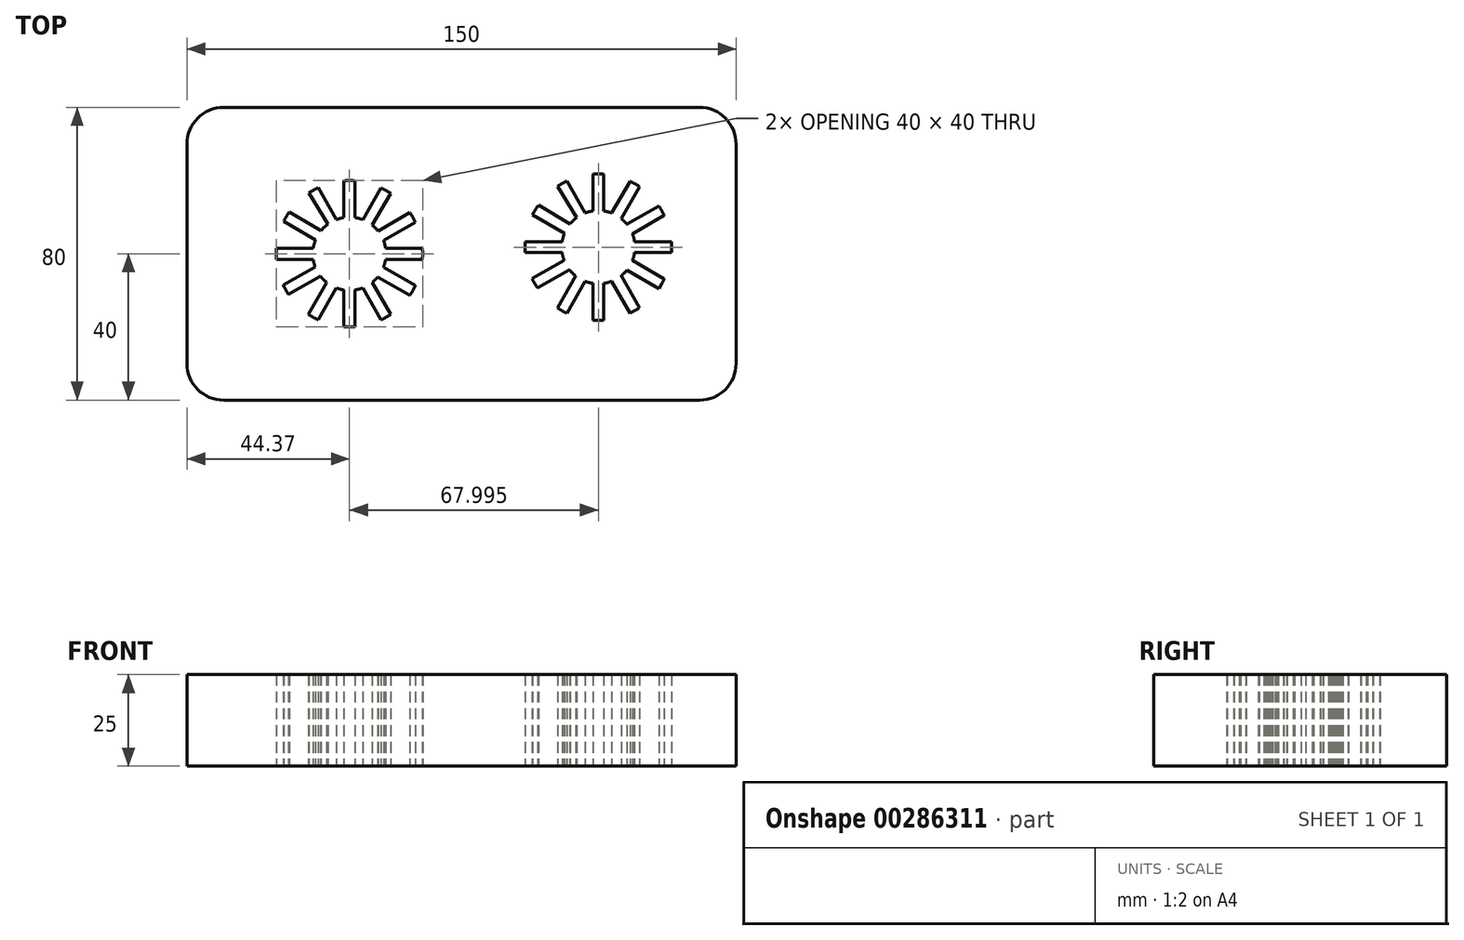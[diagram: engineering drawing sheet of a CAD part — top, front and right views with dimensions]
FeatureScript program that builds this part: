
annotation { "Feature Type Name" : "Feature", "Feature Type Description" : "" }
export const myFeature = defineFeature(function(context is Context, id is Id, definition is map)
    precondition{}
    {
        {
            var Q0;
            Q0=qCreatedBy(makeId("Top.planeOp"),FACE);
            var sketch = newSketch(context, id + "F0", { "sketchPlane" : qUnion([Q0])});
            skArc(sketch, "E0", {"start": v(-16.39, 11.46) * mm, "mid": v(-17.2, 10.2) * mm, "end": v(-17.92, 8.89) * mm});
            skCircle(sketch, "E1", {"center": v(0, 0) * mm, "radius": 10 * mm});
            skLineSegment(sketch, "E2", {"start": v(-9.86, 17.4) * mm, "end": v(-11.13, 16.61) * mm});
            skLineSegment(sketch, "E3", {"start": v(-11.13, 16.61) * mm, "end": v(-5.88, 8.1) * mm});
            skLineSegment(sketch, "E4", {"start": v(-9.86, 17.4) * mm, "end": v(-8.53, 18.1) * mm});
            skLineSegment(sketch, "E5", {"start": v(-8.53, 18.1) * mm, "end": v(-3.57, 9.34) * mm});
            skLineSegment(sketch, "E6", {"start": v(-17.2, 10.2) * mm, "end": v(-16.39, 11.46) * mm});
            skLineSegment(sketch, "E7", {"start": v(-16.39, 11.46) * mm, "end": v(-7.74, 6.33) * mm});
            skLineSegment(sketch, "E8", {"start": v(-17.2, 10.2) * mm, "end": v(-17.92, 8.89) * mm});
            skLineSegment(sketch, "E9", {"start": v(-17.92, 8.89) * mm, "end": v(-9.27, 3.76) * mm});
            skLineSegment(sketch, "E10", {"start": v(-20, 0) * mm, "end": v(-19.94, 1.5) * mm});
            skLineSegment(sketch, "E11", {"start": v(-19.94, 1.5) * mm, "end": v(-9.89, 1.5) * mm});
            skLineSegment(sketch, "E12", {"start": v(-20, 0) * mm, "end": v(-19.94, -1.5) * mm});
            skLineSegment(sketch, "E13", {"start": v(-19.94, -1.5) * mm, "end": v(-9.89, -1.5) * mm});
            skLineSegment(sketch, "E14", {"start": v(-17.4, -9.85) * mm, "end": v(-18.1, -8.52) * mm});
            skLineSegment(sketch, "E15", {"start": v(-18.1, -8.52) * mm, "end": v(-9.34, -3.56) * mm});
            skLineSegment(sketch, "E16", {"start": v(-17.4, -9.85) * mm, "end": v(-16.62, -11.12) * mm});
            skLineSegment(sketch, "E17", {"start": v(-16.62, -11.12) * mm, "end": v(-7.87, -6.17) * mm});
            skLineSegment(sketch, "E18", {"start": v(-9.9, -17.38) * mm, "end": v(-11.17, -16.59) * mm});
            skLineSegment(sketch, "E19", {"start": v(-11.17, -16.59) * mm, "end": v(-9.9, -17.38) * mm});
            skLineSegment(sketch, "E20", {"start": v(-9.9, -17.38) * mm, "end": v(-8.57, -18.07) * mm});
            skLineSegment(sketch, "E21", {"start": v(-8.57, -18.07) * mm, "end": v(-3.59, -9.33) * mm});
            skLineSegment(sketch, "E22", {"start": v(-11.17, -16.59) * mm, "end": v(-6.2, -7.85) * mm});
            skLineSegment(sketch, "E23", {"start": v(0, -20) * mm, "end": v(-1.5, -19.94) * mm});
            skLineSegment(sketch, "E24", {"start": v(0, -20) * mm, "end": v(1.5, -19.94) * mm});
            skLineSegment(sketch, "E25", {"start": v(1.5, -19.94) * mm, "end": v(1.5, -9.89) * mm});
            skLineSegment(sketch, "E26", {"start": v(-1.5, -19.94) * mm, "end": v(-1.5, -9.89) * mm});
            skArc(sketch, "E27.trimOffspring", {"start": v(-19.94, 1.5) * mm, "mid": v(-20, 0) * mm, "end": v(-19.94, -1.5) * mm});
            skArc(sketch, "E28.trimOffspring", {"start": v(-18.1, -8.52) * mm, "mid": v(-17.4, -9.85) * mm, "end": v(-16.62, -11.12) * mm});
            skArc(sketch, "E29.trimOffspring", {"start": v(-11.17, -16.59) * mm, "mid": v(-9.9, -17.38) * mm, "end": v(-8.57, -18.07) * mm});
            skArc(sketch, "E30.trimOffspring", {"start": v(-1.5, -19.94) * mm, "mid": v(0, -20) * mm, "end": v(1.5, -19.94) * mm});
            skLineSegment(sketch, "E31", {"start": v(0, 20) * mm, "end": v(-1.5, 19.94) * mm});
            skLineSegment(sketch, "E32", {"start": v(0, 20) * mm, "end": v(1.5, 19.94) * mm});
            skLineSegment(sketch, "E33", {"start": v(1.5, 19.94) * mm, "end": v(1.5, 9.89) * mm});
            skLineSegment(sketch, "E34", {"start": v(-1.5, 19.94) * mm, "end": v(-1.5, 9.89) * mm});
            skLineSegment(sketch, "E35", {"start": v(10, 17.32) * mm, "end": v(8.67, 18.02) * mm});
            skLineSegment(sketch, "E36", {"start": v(10, 17.32) * mm, "end": v(11.27, 16.52) * mm});
            skLineSegment(sketch, "E37", {"start": v(11.27, 16.52) * mm, "end": v(6.24, 7.81) * mm});
            skLineSegment(sketch, "E38", {"start": v(8.67, 18.02) * mm, "end": v(3.65, 9.31) * mm});
            skLineSegment(sketch, "E39", {"start": v(17.32, 10) * mm, "end": v(16.52, 11.27) * mm});
            skLineSegment(sketch, "E40", {"start": v(16.52, 11.27) * mm, "end": v(17.32, 10) * mm});
            skLineSegment(sketch, "E41", {"start": v(17.32, 10) * mm, "end": v(18.02, 8.67) * mm});
            skLineSegment(sketch, "E42", {"start": v(18.02, 8.67) * mm, "end": v(9.31, 3.65) * mm});
            skLineSegment(sketch, "E43", {"start": v(16.52, 11.27) * mm, "end": v(7.81, 6.24) * mm});
            skLineSegment(sketch, "E44", {"start": v(20, 0) * mm, "end": v(19.94, 1.5) * mm});
            skLineSegment(sketch, "E45", {"start": v(19.94, 1.5) * mm, "end": v(20, 0) * mm});
            skLineSegment(sketch, "E46", {"start": v(20, 0) * mm, "end": v(19.94, -1.5) * mm});
            skLineSegment(sketch, "E47", {"start": v(19.94, -1.5) * mm, "end": v(9.89, -1.5) * mm});
            skLineSegment(sketch, "E48", {"start": v(19.94, 1.5) * mm, "end": v(9.89, 1.5) * mm});
            skLineSegment(sketch, "E49", {"start": v(17.32, -10) * mm, "end": v(18.02, -8.67) * mm});
            skLineSegment(sketch, "E50", {"start": v(18.02, -8.67) * mm, "end": v(17.32, -10) * mm});
            skLineSegment(sketch, "E51", {"start": v(17.32, -10) * mm, "end": v(16.52, -11.38) * mm});
            skLineSegment(sketch, "E52", {"start": v(16.52, -11.38) * mm, "end": v(7.75, -6.32) * mm});
            skLineSegment(sketch, "E53", {"start": v(18.02, -8.67) * mm, "end": v(9.31, -3.65) * mm});
            skLineSegment(sketch, "E54", {"start": v(10, -17.32) * mm, "end": v(11.27, -16.52) * mm});
            skLineSegment(sketch, "E55", {"start": v(10, -17.32) * mm, "end": v(8.67, -18.02) * mm});
            skLineSegment(sketch, "E56", {"start": v(8.67, -18.02) * mm, "end": v(3.65, -9.31) * mm});
            skLineSegment(sketch, "E57", {"start": v(11.27, -16.52) * mm, "end": v(6.24, -7.81) * mm});
            skArc(sketch, "E58.trimOffspring", {"start": v(-8.53, 18.1) * mm, "mid": v(-9.86, 17.4) * mm, "end": v(-11.13, 16.61) * mm});
            skArc(sketch, "E59.trimOffspring", {"start": v(1.5, 19.94) * mm, "mid": v(0, 20) * mm, "end": v(-1.5, 19.94) * mm});
            skArc(sketch, "E60.trimOffspring", {"start": v(11.27, 16.52) * mm, "mid": v(10, 17.32) * mm, "end": v(8.67, 18.02) * mm});
            skArc(sketch, "E61.trimOffspring", {"start": v(18.02, 8.67) * mm, "mid": v(17.32, 10) * mm, "end": v(16.52, 11.27) * mm});
            skArc(sketch, "E62.trimOffspring", {"start": v(19.94, -1.5) * mm, "mid": v(20, 0) * mm, "end": v(19.94, 1.5) * mm});
            skArc(sketch, "E63.trimOffspring", {"start": v(16.47, -11.35) * mm, "mid": v(17.3, -10.04) * mm, "end": v(18.02, -8.67) * mm});
            skArc(sketch, "E64.trimOffspring", {"start": v(8.67, -18.02) * mm, "mid": v(10, -17.32) * mm, "end": v(11.27, -16.52) * mm});
            skLineSegment(sketch, "E65", {"start": v(0, 0) * mm, "end": v(-44.37, 0) * mm});
            skLineSegment(sketch, "E66", {"start": v(-44.37, 0) * mm, "end": v(-44.37, -30) * mm});
            skLineSegment(sketch, "E67", {"start": v(-34.37, -40) * mm, "end": v(95.63, -40) * mm});
            skLineSegment(sketch, "E68", {"start": v(105.63, -30) * mm, "end": v(105.63, 30) * mm});
            skLineSegment(sketch, "E69", {"start": v(95.63, 40) * mm, "end": v(-34.37, 40) * mm});
            skLineSegment(sketch, "E70", {"start": v(-44.37, 30) * mm, "end": v(-44.37, 0) * mm});
            skPoint(sketch, "E71.visualSharp", {"position": v(-44.37, 40) * mm});
            skArc(sketch, "E71.filletArc", {"start": v(-34.37, 40) * mm, "mid": v(-41.44, 37.07) * mm, "end": v(-44.37, 30) * mm});
            skPoint(sketch, "E72.visualSharp", {"position": v(-44.37, -40) * mm});
            skArc(sketch, "E72.filletArc", {"start": v(-44.37, -30) * mm, "mid": v(-41.44, -37.07) * mm, "end": v(-34.37, -40) * mm});
            skPoint(sketch, "E73.visualSharp", {"position": v(105.63, 40) * mm});
            skArc(sketch, "E73.filletArc", {"start": v(105.63, 30) * mm, "mid": v(102.7, 37.07) * mm, "end": v(95.63, 40) * mm});
            skPoint(sketch, "E74.visualSharp", {"position": v(105.63, -40) * mm});
            skArc(sketch, "E74.filletArc", {"start": v(95.63, -40) * mm, "mid": v(102.7, -37.07) * mm, "end": v(105.63, -30) * mm});
            skArc(sketch, "E75", {"start": v(51.6, 13.27) * mm, "mid": v(50.8, 12.01) * mm, "end": v(50.08, 10.7) * mm});
            skCircle(sketch, "E76", {"center": v(68, 1.8) * mm, "radius": 10 * mm});
            skLineSegment(sketch, "E77", {"start": v(68, -8.2) * mm, "end": v(68, 11.8) * mm});
            skLineSegment(sketch, "E78", {"start": v(58, 1.8) * mm, "end": v(78, 1.8) * mm});
            skLineSegment(sketch, "E79", {"start": v(58.14, 19.2) * mm, "end": v(56.86, 18.42) * mm});
            skLineSegment(sketch, "E80", {"start": v(56.86, 18.42) * mm, "end": v(62.12, 9.9) * mm});
            skLineSegment(sketch, "E81", {"start": v(58.14, 19.2) * mm, "end": v(59.47, 19.9) * mm});
            skLineSegment(sketch, "E82", {"start": v(59.47, 19.9) * mm, "end": v(64.43, 11.15) * mm});
            skLineSegment(sketch, "E83", {"start": v(50.8, 12.01) * mm, "end": v(51.6, 13.27) * mm});
            skLineSegment(sketch, "E84", {"start": v(51.6, 13.27) * mm, "end": v(60.26, 8.14) * mm});
            skLineSegment(sketch, "E85", {"start": v(50.8, 12.01) * mm, "end": v(50.08, 10.7) * mm});
            skLineSegment(sketch, "E86", {"start": v(50.08, 10.7) * mm, "end": v(58.73, 5.56) * mm});
            skLineSegment(sketch, "E87", {"start": v(48, 1.8) * mm, "end": v(48.05, 3.3) * mm});
            skLineSegment(sketch, "E88", {"start": v(48.05, 3.3) * mm, "end": v(58.1, 3.3) * mm});
            skLineSegment(sketch, "E89", {"start": v(48, 1.8) * mm, "end": v(48.05, 0.3) * mm});
            skLineSegment(sketch, "E90", {"start": v(48.05, 0.3) * mm, "end": v(58.1, 0.3) * mm});
            skLineSegment(sketch, "E91", {"start": v(68, 1.8) * mm, "end": v(63.05, -6.88) * mm});
            skLineSegment(sketch, "E92", {"start": v(50.59, -8.04) * mm, "end": v(49.9, -6.7) * mm});
            skLineSegment(sketch, "E93", {"start": v(49.9, -6.7) * mm, "end": v(58.65, -1.76) * mm});
            skLineSegment(sketch, "E94", {"start": v(50.59, -8.04) * mm, "end": v(51.37, -9.32) * mm});
            skLineSegment(sketch, "E95", {"start": v(51.37, -9.32) * mm, "end": v(60.13, -4.37) * mm});
            skLineSegment(sketch, "E96", {"start": v(58.1, -15.57) * mm, "end": v(56.82, -14.78) * mm});
            skLineSegment(sketch, "E97", {"start": v(56.82, -14.78) * mm, "end": v(58.1, -15.57) * mm});
            skLineSegment(sketch, "E98", {"start": v(58.1, -15.57) * mm, "end": v(59.43, -16.27) * mm});
            skLineSegment(sketch, "E99", {"start": v(59.43, -16.27) * mm, "end": v(64.4, -7.53) * mm});
            skLineSegment(sketch, "E100", {"start": v(56.82, -14.78) * mm, "end": v(61.8, -6.04) * mm});
            skLineSegment(sketch, "E101", {"start": v(68, -18.2) * mm, "end": v(66.5, -18.14) * mm});
            skLineSegment(sketch, "E102", {"start": v(68, -18.2) * mm, "end": v(69.5, -18.14) * mm});
            skLineSegment(sketch, "E103", {"start": v(69.5, -18.14) * mm, "end": v(69.5, -8.08) * mm});
            skLineSegment(sketch, "E104", {"start": v(66.5, -18.14) * mm, "end": v(66.5, -8.08) * mm});
            skArc(sketch, "E105.trimOffspring", {"start": v(48.05, 3.3) * mm, "mid": v(48, 1.8) * mm, "end": v(48.05, 0.3) * mm});
            skArc(sketch, "E106.trimOffspring", {"start": v(49.9, -6.7) * mm, "mid": v(50.59, -8.04) * mm, "end": v(51.37, -9.32) * mm});
            skArc(sketch, "E107.trimOffspring", {"start": v(56.82, -14.78) * mm, "mid": v(58.1, -15.57) * mm, "end": v(59.43, -16.27) * mm});
            skArc(sketch, "E108.trimOffspring", {"start": v(66.5, -18.14) * mm, "mid": v(68, -18.2) * mm, "end": v(69.5, -18.14) * mm});
            skLineSegment(sketch, "E109", {"start": v(68, 21.8) * mm, "end": v(66.5, 21.75) * mm});
            skLineSegment(sketch, "E110", {"start": v(68, 21.8) * mm, "end": v(69.5, 21.75) * mm});
            skLineSegment(sketch, "E111", {"start": v(69.5, 21.75) * mm, "end": v(69.5, 11.7) * mm});
            skLineSegment(sketch, "E112", {"start": v(66.5, 21.75) * mm, "end": v(66.5, 11.7) * mm});
            skLineSegment(sketch, "E113", {"start": v(68, 1.8) * mm, "end": v(73, 10.47) * mm});
            skLineSegment(sketch, "E114", {"start": v(68, 1.8) * mm, "end": v(76.65, 6.8) * mm});
            skLineSegment(sketch, "E115", {"start": v(68, 1.8) * mm, "end": v(76.65, -3.2) * mm});
            skLineSegment(sketch, "E116", {"start": v(68, 1.8) * mm, "end": v(73, -6.85) * mm});
            skLineSegment(sketch, "E117", {"start": v(78, 19.13) * mm, "end": v(76.67, 19.83) * mm});
            skLineSegment(sketch, "E118", {"start": v(78, 19.13) * mm, "end": v(79.26, 18.33) * mm});
            skLineSegment(sketch, "E119", {"start": v(79.26, 18.33) * mm, "end": v(74.24, 9.62) * mm});
            skLineSegment(sketch, "E120", {"start": v(76.67, 19.83) * mm, "end": v(71.64, 11.12) * mm});
            skLineSegment(sketch, "E121", {"start": v(85.32, 11.8) * mm, "end": v(84.52, 13.08) * mm});
            skLineSegment(sketch, "E122", {"start": v(84.52, 13.08) * mm, "end": v(85.32, 11.8) * mm});
            skLineSegment(sketch, "E123", {"start": v(85.32, 11.8) * mm, "end": v(86.02, 10.48) * mm});
            skLineSegment(sketch, "E124", {"start": v(86.02, 10.48) * mm, "end": v(77.3, 5.45) * mm});
            skLineSegment(sketch, "E125", {"start": v(84.52, 13.08) * mm, "end": v(75.8, 8.05) * mm});
            skLineSegment(sketch, "E126", {"start": v(88, 1.8) * mm, "end": v(87.94, 3.3) * mm});
            skLineSegment(sketch, "E127", {"start": v(87.94, 3.3) * mm, "end": v(88, 1.8) * mm});
            skLineSegment(sketch, "E128", {"start": v(88, 1.8) * mm, "end": v(87.94, 0.3) * mm});
            skLineSegment(sketch, "E129", {"start": v(87.94, 0.3) * mm, "end": v(77.88, 0.3) * mm});
            skLineSegment(sketch, "E130", {"start": v(87.94, 3.3) * mm, "end": v(77.88, 3.3) * mm});
            skLineSegment(sketch, "E131", {"start": v(85.32, -8.2) * mm, "end": v(86.02, -6.87) * mm});
            skLineSegment(sketch, "E132", {"start": v(86.02, -6.87) * mm, "end": v(85.32, -8.2) * mm});
            skLineSegment(sketch, "E133", {"start": v(85.32, -8.2) * mm, "end": v(84.52, -9.58) * mm});
            skLineSegment(sketch, "E134", {"start": v(84.52, -9.58) * mm, "end": v(75.75, -4.51) * mm});
            skLineSegment(sketch, "E135", {"start": v(86.02, -6.87) * mm, "end": v(77.3, -1.84) * mm});
            skLineSegment(sketch, "E136", {"start": v(78, -15.51) * mm, "end": v(79.26, -14.72) * mm});
            skLineSegment(sketch, "E137", {"start": v(78, -15.51) * mm, "end": v(76.67, -16.22) * mm});
            skLineSegment(sketch, "E138", {"start": v(76.67, -16.22) * mm, "end": v(71.64, -7.5) * mm});
            skLineSegment(sketch, "E139", {"start": v(79.26, -14.72) * mm, "end": v(74.24, -6) * mm});
            skArc(sketch, "E140.trimOffspring", {"start": v(59.47, 19.9) * mm, "mid": v(58.14, 19.2) * mm, "end": v(56.86, 18.42) * mm});
            skArc(sketch, "E141.trimOffspring", {"start": v(69.5, 21.75) * mm, "mid": v(68, 21.8) * mm, "end": v(66.5, 21.75) * mm});
            skArc(sketch, "E142.trimOffspring", {"start": v(79.26, 18.33) * mm, "mid": v(78, 19.13) * mm, "end": v(76.67, 19.83) * mm});
            skArc(sketch, "E143.trimOffspring", {"start": v(86.02, 10.48) * mm, "mid": v(85.32, 11.8) * mm, "end": v(84.52, 13.08) * mm});
            skArc(sketch, "E144.trimOffspring", {"start": v(87.94, 0.3) * mm, "mid": v(88, 1.8) * mm, "end": v(87.94, 3.3) * mm});
            skArc(sketch, "E145.trimOffspring", {"start": v(84.46, -9.54) * mm, "mid": v(85.3, -8.24) * mm, "end": v(86.02, -6.87) * mm});
            skArc(sketch, "E146.trimOffspring", {"start": v(76.67, -16.22) * mm, "mid": v(78, -15.51) * mm, "end": v(79.26, -14.72) * mm});
            skSolve(sketch);
        }
        {
            var Q0;
            Q0 = qSketchRegion(id + "F0", true);
            extrude(context, id + "F1", {"entities" : qUnion([Q0]), "depth" : 25 * mm});
        }
    });
